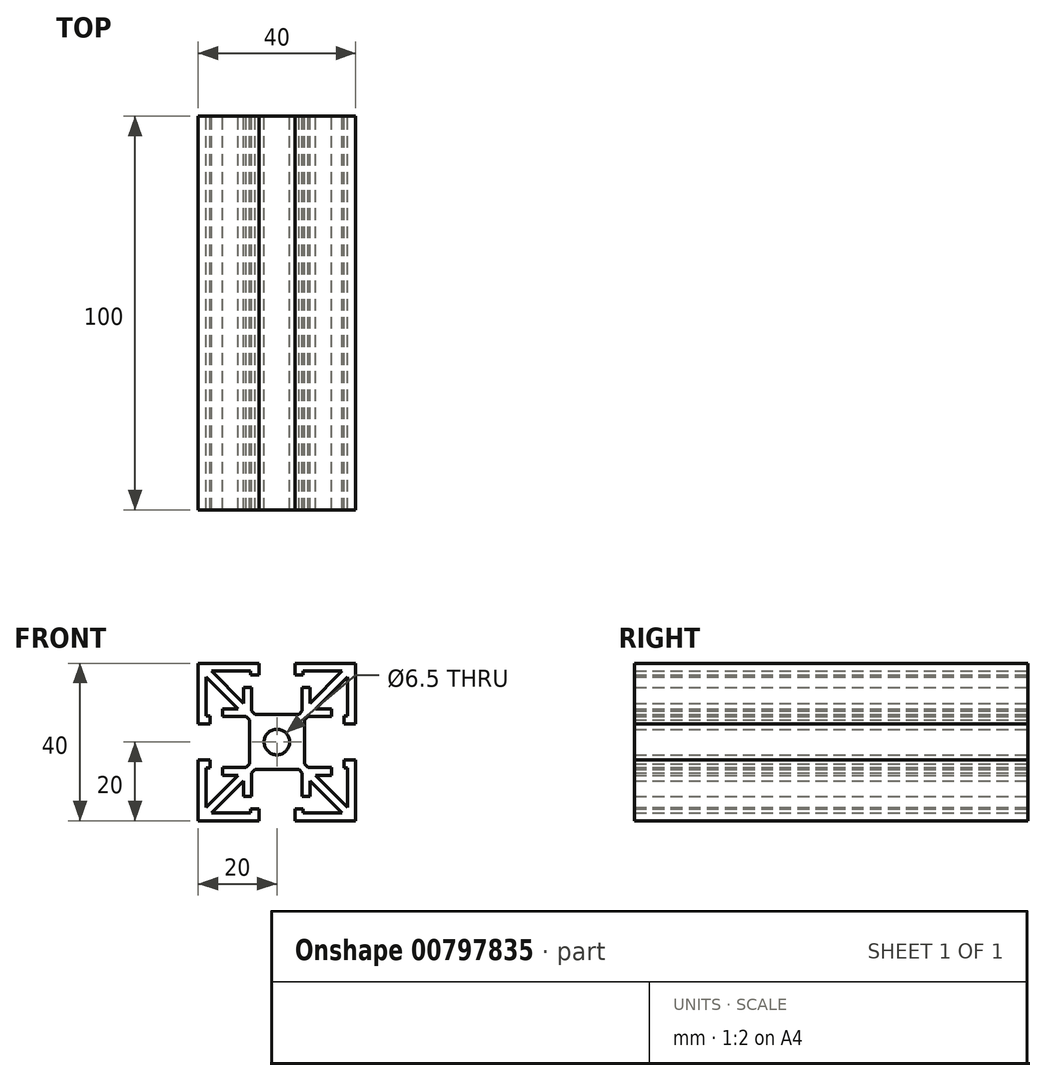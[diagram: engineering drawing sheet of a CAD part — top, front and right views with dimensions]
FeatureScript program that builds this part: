
annotation { "Feature Type Name" : "Feature", "Feature Type Description" : "" }
export const myFeature = defineFeature(function(context is Context, id is Id, definition is map)
    precondition{}
    {
        {
            var Q0;
            Q0=qCreatedBy(makeId("Front.planeOp"),FACE);
            var sketch = newSketch(context, id + "F0", { "sketchPlane" : qUnion([Q0])});
            skLineSegment(sketch, "E0.bottom", {"start": v(0, 0) * mm, "end": v(15.43, 0) * mm});
            skLineSegment(sketch, "E1", {"start": v(0, 0) * mm, "end": v(0, 15.43) * mm});
            skArc(sketch, "E2", {"start": v(16.75, 20) * mm, "mid": v(17.7, 17.7) * mm, "end": v(20, 16.75) * mm});
            skLineSegment(sketch, "E3.top", {"start": v(20, 13) * mm, "end": v(14.41, 13) * mm});
            skLineSegment(sketch, "E3.right", {"start": v(13, 20) * mm, "end": v(13, 14.41) * mm});
            skLineSegment(sketch, "E4", {"start": v(20, 13) * mm, "end": v(20, 16.75) * mm});
            skLineSegment(sketch, "E5", {"start": v(13, 20) * mm, "end": v(16.75, 20) * mm});
            skLineSegment(sketch, "E6", {"start": v(2, 3.41) * mm, "end": v(10.14, 11.55) * mm});
            skLineSegment(sketch, "E7", {"start": v(14.41, 13) * mm, "end": v(13.55, 12.14) * mm});
            skLineSegment(sketch, "E8", {"start": v(12.14, 13.55) * mm, "end": v(6.14, 13.55) * mm});
            skLineSegment(sketch, "E9", {"start": v(6.14, 13.55) * mm, "end": v(6.14, 11.55) * mm});
            skLineSegment(sketch, "E10", {"start": v(6.14, 11.55) * mm, "end": v(10.14, 11.55) * mm});
            skLineSegment(sketch, "E11.trimOffspring", {"start": v(12.14, 13.55) * mm, "end": v(13, 14.41) * mm});
            skLineSegment(sketch, "E12", {"start": v(13.55, 12.14) * mm, "end": v(13.55, 6.14) * mm});
            skLineSegment(sketch, "E13", {"start": v(13.55, 6.14) * mm, "end": v(11.55, 6.14) * mm});
            skLineSegment(sketch, "E14", {"start": v(11.55, 6.14) * mm, "end": v(11.55, 10.14) * mm});
            skLineSegment(sketch, "E15.trimOffspring", {"start": v(11.55, 10.14) * mm, "end": v(3.41, 2) * mm});
            skLineSegment(sketch, "E16", {"start": v(15.43, 0) * mm, "end": v(15.43, 3) * mm});
            skLineSegment(sketch, "E17", {"start": v(15.43, 3) * mm, "end": v(13.36, 3) * mm});
            skLineSegment(sketch, "E18", {"start": v(3.41, 2) * mm, "end": v(13.36, 2) * mm});
            skLineSegment(sketch, "E19", {"start": v(13.36, 2) * mm, "end": v(13.36, 3) * mm});
            skLineSegment(sketch, "E20", {"start": v(0, 15.43) * mm, "end": v(3, 15.43) * mm});
            skLineSegment(sketch, "E21", {"start": v(3, 15.43) * mm, "end": v(3, 13.36) * mm});
            skLineSegment(sketch, "E22", {"start": v(3, 13.36) * mm, "end": v(2, 13.36) * mm});
            skLineSegment(sketch, "E23", {"start": v(2, 13.36) * mm, "end": v(2, 3.41) * mm});
            skSolve(sketch);
        }
        {
            var Q0;
            Q0=makeQuery(id+"F0.imprint","IMPRINT",FACE,{"disambiguationData":[TD([[makeQuery(id+"F0.imprint","IMPRINT",EDGE,{"derivedFrom":sQuery(id+"F0.wireOp",EDGE,"E0.bottom")}),1.0]])]});
            extrude(context, id + "F1", {"entities" : qUnion([Q0]), "depth" : 100 * mm, "offsetDistance" : 25 * mm});
        }
        {
            var Q0;
            Q0=makeQuery(id+"F1.opExtrude","SWEPT_BODY",BODY,{"disambiguationData":[OSD([sQuery(id+"F0.wireOp",EDGE,"E0.bottom"),sQuery(id+"F0.wireOp",EDGE,"bxMyjKEQ-UYGA-28RK-UkX0-PHLreR1HHNFS"),sQuery(id+"F0.wireOp",EDGE,"E1"),sQuery(id+"F0.wireOp",EDGE,"oHsMIj1o-Qbf1-A1nL-iEAP-f7QsIZkSYNUt"),sQuery(id+"F0.wireOp",EDGE,"0hIzz6Nh-Sauq-4LEg-K3Cd-crla56emVGup"),sQuery(id+"F0.wireOp",EDGE,"Mzx24WrW-U7Hr-yIYI-P811-encKqDaWsp3P"),sQuery(id+"F0.wireOp",EDGE,"E2"),sQuery(id+"F0.wireOp",EDGE,"E3.top"),sQuery(id+"F0.wireOp",EDGE,"E3.right"),sQuery(id+"F0.wireOp",EDGE,"E4"),sQuery(id+"F0.wireOp",EDGE,"E5"),sQuery(id+"F0.wireOp",EDGE,"E6"),sQuery(id+"F0.wireOp",EDGE,"E7"),sQuery(id+"F0.wireOp",EDGE,"E8"),sQuery(id+"F0.wireOp",EDGE,"E9"),sQuery(id+"F0.wireOp",EDGE,"E10"),sQuery(id+"F0.wireOp",EDGE,"E11.trimOffspring"),sQuery(id+"F0.wireOp",EDGE,"E12"),sQuery(id+"F0.wireOp",EDGE,"E13"),sQuery(id+"F0.wireOp",EDGE,"E14"),sQuery(id+"F0.wireOp",EDGE,"E15.trimOffspring")])]});
            var Q1;
            Q1=makeQuery(id+"F1.opExtrude","SWEPT_FACE",FACE,{"disambiguationData":[OSD([sQuery(id+"F0.wireOp",EDGE,"E4")])]});
            mirror(context, id + "F2", {"operationType" : NewBodyOperationType.ADD, "entities" : qUnion([Q0]), "mirrorPlane" : qUnion([Q1])});
        }
        {
            var Q0;
            Q0=makeQuery(id+"F1.opExtrude","SWEPT_BODY",BODY,{"disambiguationData":[OSD([sQuery(id+"F0.wireOp",EDGE,"E0.bottom"),sQuery(id+"F0.wireOp",EDGE,"bxMyjKEQ-UYGA-28RK-UkX0-PHLreR1HHNFS"),sQuery(id+"F0.wireOp",EDGE,"E1"),sQuery(id+"F0.wireOp",EDGE,"oHsMIj1o-Qbf1-A1nL-iEAP-f7QsIZkSYNUt"),sQuery(id+"F0.wireOp",EDGE,"0hIzz6Nh-Sauq-4LEg-K3Cd-crla56emVGup"),sQuery(id+"F0.wireOp",EDGE,"Mzx24WrW-U7Hr-yIYI-P811-encKqDaWsp3P"),sQuery(id+"F0.wireOp",EDGE,"E2"),sQuery(id+"F0.wireOp",EDGE,"E3.top"),sQuery(id+"F0.wireOp",EDGE,"E3.right"),sQuery(id+"F0.wireOp",EDGE,"E4"),sQuery(id+"F0.wireOp",EDGE,"E5"),sQuery(id+"F0.wireOp",EDGE,"E6"),sQuery(id+"F0.wireOp",EDGE,"E7"),sQuery(id+"F0.wireOp",EDGE,"E8"),sQuery(id+"F0.wireOp",EDGE,"E9"),sQuery(id+"F0.wireOp",EDGE,"E10"),sQuery(id+"F0.wireOp",EDGE,"E11.trimOffspring"),sQuery(id+"F0.wireOp",EDGE,"E12"),sQuery(id+"F0.wireOp",EDGE,"E13"),sQuery(id+"F0.wireOp",EDGE,"E14"),sQuery(id+"F0.wireOp",EDGE,"E15.trimOffspring")])]});
            var Q1;
            Q1=makeQuery(id+"F1.opExtrude","SWEPT_FACE",FACE,{"disambiguationData":[OSD([sQuery(id+"F0.wireOp",EDGE,"E5")])]});
            mirror(context, id + "F3", {"operationType" : NewBodyOperationType.ADD, "entities" : qUnion([Q0]), "mirrorPlane" : qUnion([Q1])});
        }
    });
